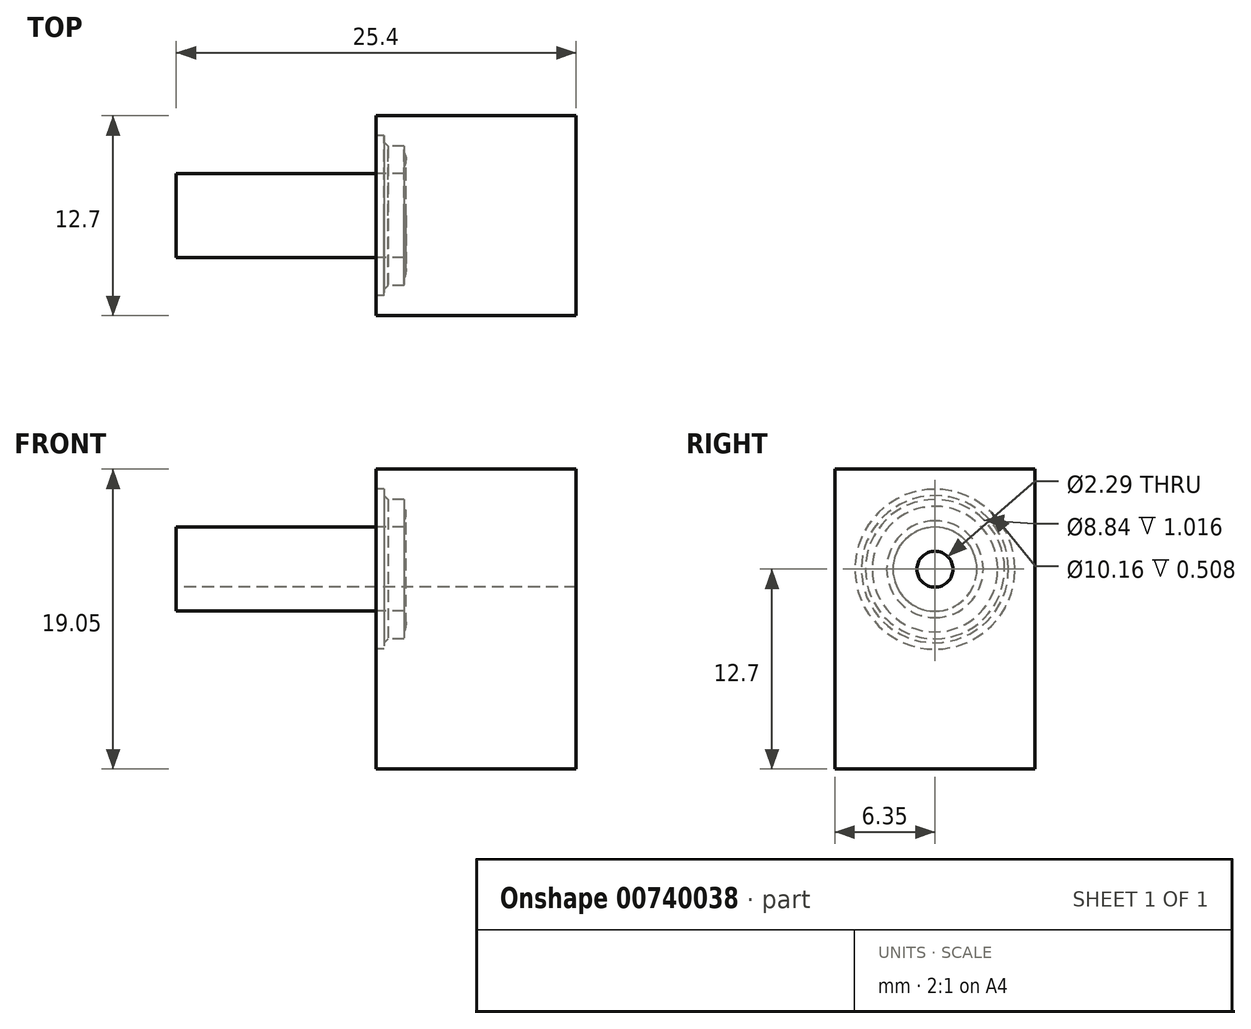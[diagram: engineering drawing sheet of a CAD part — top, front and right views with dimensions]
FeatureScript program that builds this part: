
annotation { "Feature Type Name" : "Feature", "Feature Type Description" : "" }
export const myFeature = defineFeature(function(context is Context, id is Id, definition is map)
    precondition{}
    {
        {
            var Q0;
            Q0=qCreatedBy(makeId("Right.planeOp"),FACE);
            var sketch = newSketch(context, id + "F0", { "sketchPlane" : qUnion([Q0])});
            skCircle(sketch, "E0", {"center": v(0, 0) * mm, "radius": 2.67 * mm});
            skCircle(sketch, "E1", {"center": v(0, 0) * mm, "radius": 1.14 * mm});
            skSolve(sketch);
        }
        {
            var Q0;
            Q0 = qSketchRegion(id + "F0", true);
            extrude(context, id + "F1", {"entities" : qUnion([Q0]), "depth" : 12.7 * mm, "offsetDistance" : 25.4 * mm});
        }
        {
            var Q0;
            Q0=qCreatedBy(makeId("Front.planeOp"),FACE);
            var sketch = newSketch(context, id + "F2", { "sketchPlane" : qUnion([Q0])});
            skLineSegment(sketch, "E2", {"start": v(0, 0) * mm, "end": v(36.4, 0) * mm, "construction": true});
            skSolve(sketch);
        }
        {
            var Q0;
            Q0=qCreatedBy(makeId("Front.planeOp"),FACE);
            var sketch = newSketch(context, id + "F3", { "sketchPlane" : qUnion([Q0])});
            skCircle(sketch, "E3", {"center": v(13.72, 3.53) * mm, "radius": 0.89 * mm});
            skSolve(sketch);
        }
        {
            var Q0;
            Q0 = qSketchRegion(id + "F3", true);
            var Q1;
            Q1=sQuery(id+"F2.wireOp",EDGE,"E2");
            revolve(context, id + "F4", {"surfaceOperationType" : NewSurfaceOperationType.NEW, "entities" : qUnion([Q0]), "axis" : qUnion([Q1]), "revolveType" : RevolveType.FULL});
        }
        {
            var Q0;
            Q0=makeQuery(id+"F1.opExtrude","CAP_FACE",FACE,{"disambiguationData":[OSD([sQuery(id+"F0.wireOp",EDGE,"E0"),sQuery(id+"F0.wireOp",EDGE,"E1")])],"isStart":false});
            var sketch = newSketch(context, id + "F5", { "sketchPlane" : qUnion([Q0])});
            skLineSegment(sketch, "E4.bottom", {"start": v(-6.35, 6.35) * mm, "end": v(6.35, 6.35) * mm});
            skLineSegment(sketch, "E4.top", {"start": v(-6.35, -12.7) * mm, "end": v(6.35, -12.7) * mm});
            skLineSegment(sketch, "E4.left", {"start": v(-6.35, 6.35) * mm, "end": v(-6.35, -12.7) * mm});
            skLineSegment(sketch, "E4.right", {"start": v(6.35, 6.35) * mm, "end": v(6.35, -12.7) * mm});
            skSolve(sketch);
        }
        {
            var Q0;
            Q0 = qSketchRegion(id + "F5", true);
            extrude(context, id + "F6", {"entities" : qUnion([Q0]), "depth" : 12.7 * mm, "offsetDistance" : 25.4 * mm});
        }
        {
            var Q0;
            Q0=makeQuery(id+"F6.opExtrude","CAP_FACE",FACE,{"disambiguationData":[OSD([sQuery(id+"F5.wireOp",EDGE,"E4.bottom"),sQuery(id+"F5.wireOp",EDGE,"E4.top"),sQuery(id+"F5.wireOp",EDGE,"E4.left"),sQuery(id+"F5.wireOp",EDGE,"E4.right")])],"isStart":true});
            var sketch = newSketch(context, id + "F7", { "sketchPlane" : qUnion([Q0])});
            skCircle(sketch, "E5", {"center": v(0, 0) * mm, "radius": 2.67 * mm});
            skSolve(sketch);
        }
        {
            var Q0;
            Q0 = qSketchRegion(id + "F7", true);
            extrude(context, id + "F8", {"entities" : qUnion([Q0]), "operationType" : NewBodyOperationType.REMOVE, "endBound" : BoundingType.THROUGH_ALL, "oppositeDirection" : true, "depth" : 25.4 * mm, "offsetDistance" : 25.4 * mm});
        }
        {
            var Q0;
            Q0=makeQuery(id+"F6.opExtrude","CAP_FACE",FACE,{"disambiguationData":[OSD([sQuery(id+"F5.wireOp",EDGE,"E4.bottom"),sQuery(id+"F5.wireOp",EDGE,"E4.top"),sQuery(id+"F5.wireOp",EDGE,"E4.left"),sQuery(id+"F5.wireOp",EDGE,"E4.right")])],"isStart":true});
            var sketch = newSketch(context, id + "F9", { "sketchPlane" : qUnion([Q0])});
            skCircle(sketch, "E6", {"center": v(0, 0) * mm, "radius": 4.42 * mm});
            skSolve(sketch);
        }
        {
            var Q0;
            Q0 = qSketchRegion(id + "F9", true);
            extrude(context, id + "F10", {"entities" : qUnion([Q0]), "operationType" : NewBodyOperationType.REMOVE, "oppositeDirection" : true, "depth" : 1.78 * mm, "offsetDistance" : 25.4 * mm});
        }
        {
            var Q0;
            Q0=makeQuery(id+"F6.opExtrude","CAP_FACE",FACE,{"disambiguationData":[OSD([sQuery(id+"F5.wireOp",EDGE,"E4.bottom"),sQuery(id+"F5.wireOp",EDGE,"E4.top"),sQuery(id+"F5.wireOp",EDGE,"E4.left"),sQuery(id+"F5.wireOp",EDGE,"E4.right")])],"isStart":true});
            var sketch = newSketch(context, id + "F11", { "sketchPlane" : qUnion([Q0])});
            skCircle(sketch, "E7", {"center": v(0, 0) * mm, "radius": 5.08 * mm});
            skSolve(sketch);
        }
        {
            var Q0;
            Q0 = qSketchRegion(id + "F11", true);
            extrude(context, id + "F12", {"entities" : qUnion([Q0]), "operationType" : NewBodyOperationType.REMOVE, "oppositeDirection" : true, "depth" : 0.5 * mm, "offsetDistance" : 25.4 * mm});
        }
        {
            var Q0;
            Q0=makeQuery(id+"F12.boolean.opBoolean","COPY",EDGE,{"derivedFrom":makeQuery(id+"F12.opExtrude","CAP_EDGE",EDGE,{"disambiguationData":[OSD([sQuery(id+"F11.wireOp",EDGE,"E7")])],"isStart":true})});
            var Q1;
            Q1=makeQuery(id+"F12.boolean.opBoolean","INTERSECT",EDGE,{"derivedFrom":[makeQuery(id+"F10.boolean.opBoolean","COPY",FACE,{"derivedFrom":makeQuery(id+"F10.opExtrude","SWEPT_FACE",FACE,{"disambiguationData":[OSD([sQuery(id+"F9.wireOp",EDGE,"E6")])]})}),makeQuery(id+"F12.opExtrude","CAP_FACE",FACE,{"disambiguationData":[OSD([sQuery(id+"F11.wireOp",EDGE,"E7")])],"isStart":false})]});
            chamfer(context, id + "F13", {"entities" : qUnion([Q0, Q1]), "width" : 0.25 * mm, "tangentPropagation" : true});
        }
        {
            var Q0;
            Q0=makeQuery(id+"F1.opExtrude","CAP_FACE",FACE,{"disambiguationData":[OSD([sQuery(id+"F0.wireOp",EDGE,"E0"),sQuery(id+"F0.wireOp",EDGE,"E1")])],"isStart":false});
            var sketch = newSketch(context, id + "F14", { "sketchPlane" : qUnion([Q0])});
            skCircle(sketch, "E8", {"center": v(0, 0) * mm, "radius": 1.14 * mm});
            skCircle(sketch, "E9", {"center": v(0, 0) * mm, "radius": 2.67 * mm});
            skSolve(sketch);
        }
        {
            var Q0;
            Q0 = qSketchRegion(id + "F14", true);
            extrude(context, id + "F15", {"entities" : qUnion([Q0]), "operationType" : NewBodyOperationType.ADD, "depth" : 12.7 * mm, "offsetDistance" : 25.4 * mm});
        }
    });
